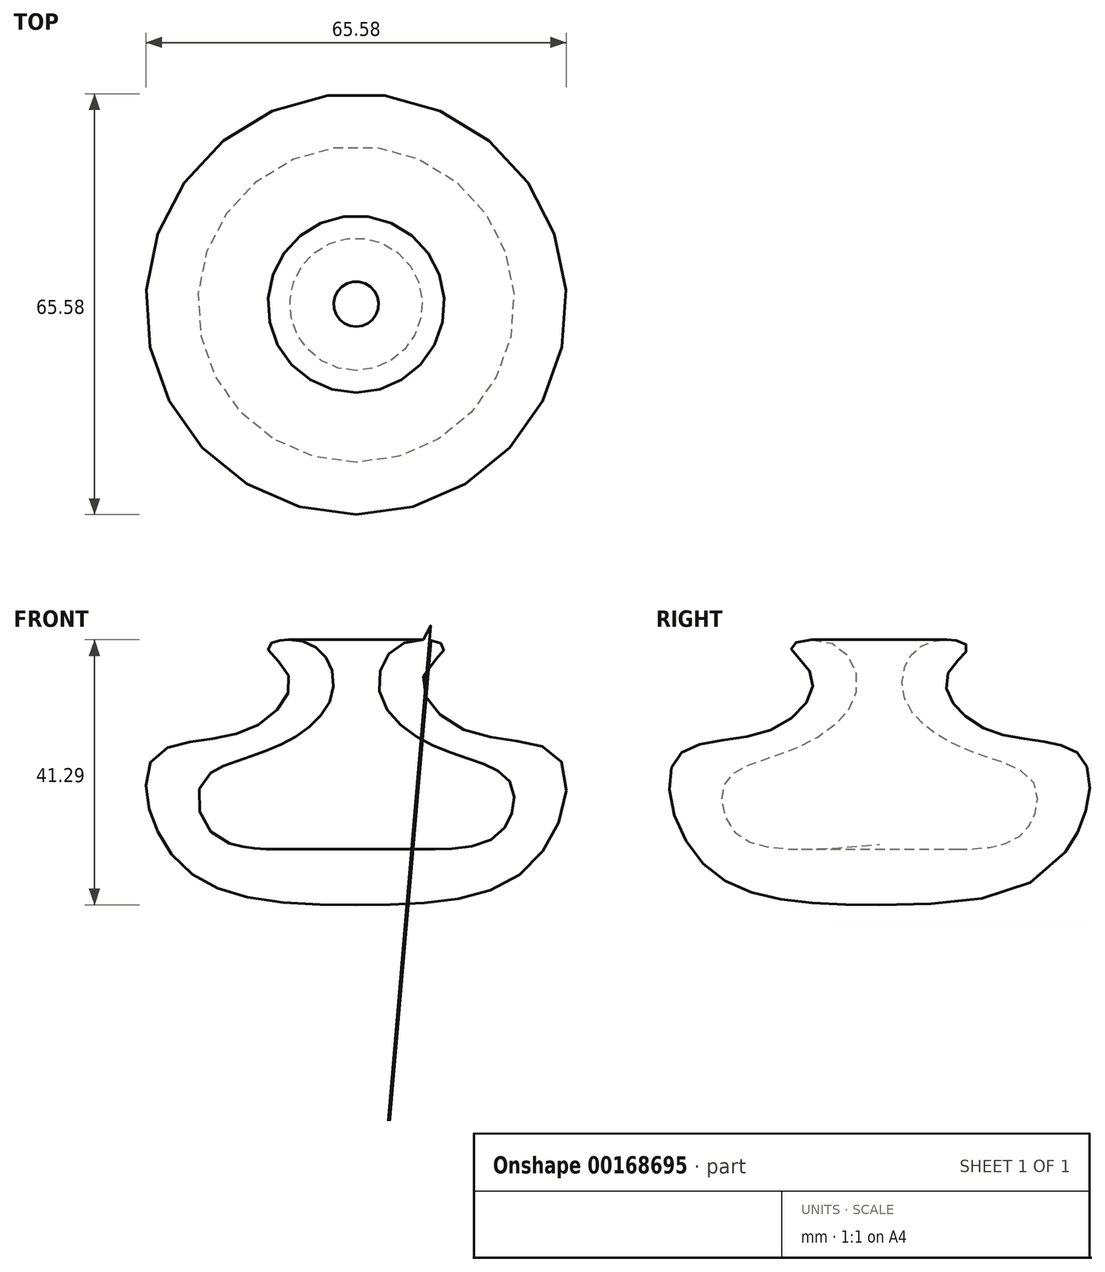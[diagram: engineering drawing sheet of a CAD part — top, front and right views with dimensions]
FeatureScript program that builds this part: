
annotation { "Feature Type Name" : "Feature", "Feature Type Description" : "" }
export const myFeature = defineFeature(function(context is Context, id is Id, definition is map)
    precondition{}
    {
        {
            var Q0;
            Q0=qCreatedBy(makeId("Right.planeOp"),FACE);
            var sketch = newSketch(context, id + "F0", { "sketchPlane" : qUnion([Q0])});
            skLineSegment(sketch, "E0", {"start": v(0, 9.42) * mm, "end": v(0, 0) * mm});
            skFitSpline(sketch, "E1", {"points": [v(0, 0) * mm, v(-27.21, 6.15) * mm, v(-31.64, 22.89) * mm, v(-17.21, 27.12) * mm, v(-10.48, 35.58) * mm, v(-13.75, 40.2) * mm, v(-7.02, 40.58) * mm, v(-3.75, 32.7) * mm, v(-11.25, 25.2) * mm, v(-19.9, 21.93) * mm, v(-24.33, 18.46) * mm, v(-22.6, 11.35) * mm, v(-13.17, 8.65) * mm, v(0, 9.42) * mm], "startDerivative": vector(-254.43, 1.38) * mm, "endDerivative": vector(156.14, 14.94) * mm});
            skSolve(sketch);
        }
        {
            var Q0;
            Q0=makeQuery(id+"F0.imprint","IMPRINT",FACE,{"disambiguationData":[TD([[makeQuery(id+"F0.imprint","IMPRINT",EDGE,{"derivedFrom":sQuery(id+"F0.wireOp",EDGE,"E0")}),-1.0]])]});
            var Q1;
            Q1=sQuery(id+"F0.wireOp",EDGE,"E0");
            var Q2;
            Q2=sQuery(id+"F0.wireOp",EDGE,"E0");
            revolve(context, id + "F1", {"entities" : qUnion([Q0]), "axis" : qUnion([Q1, Q2]), "revolveType" : RevolveType.FULL});
        }
    });
